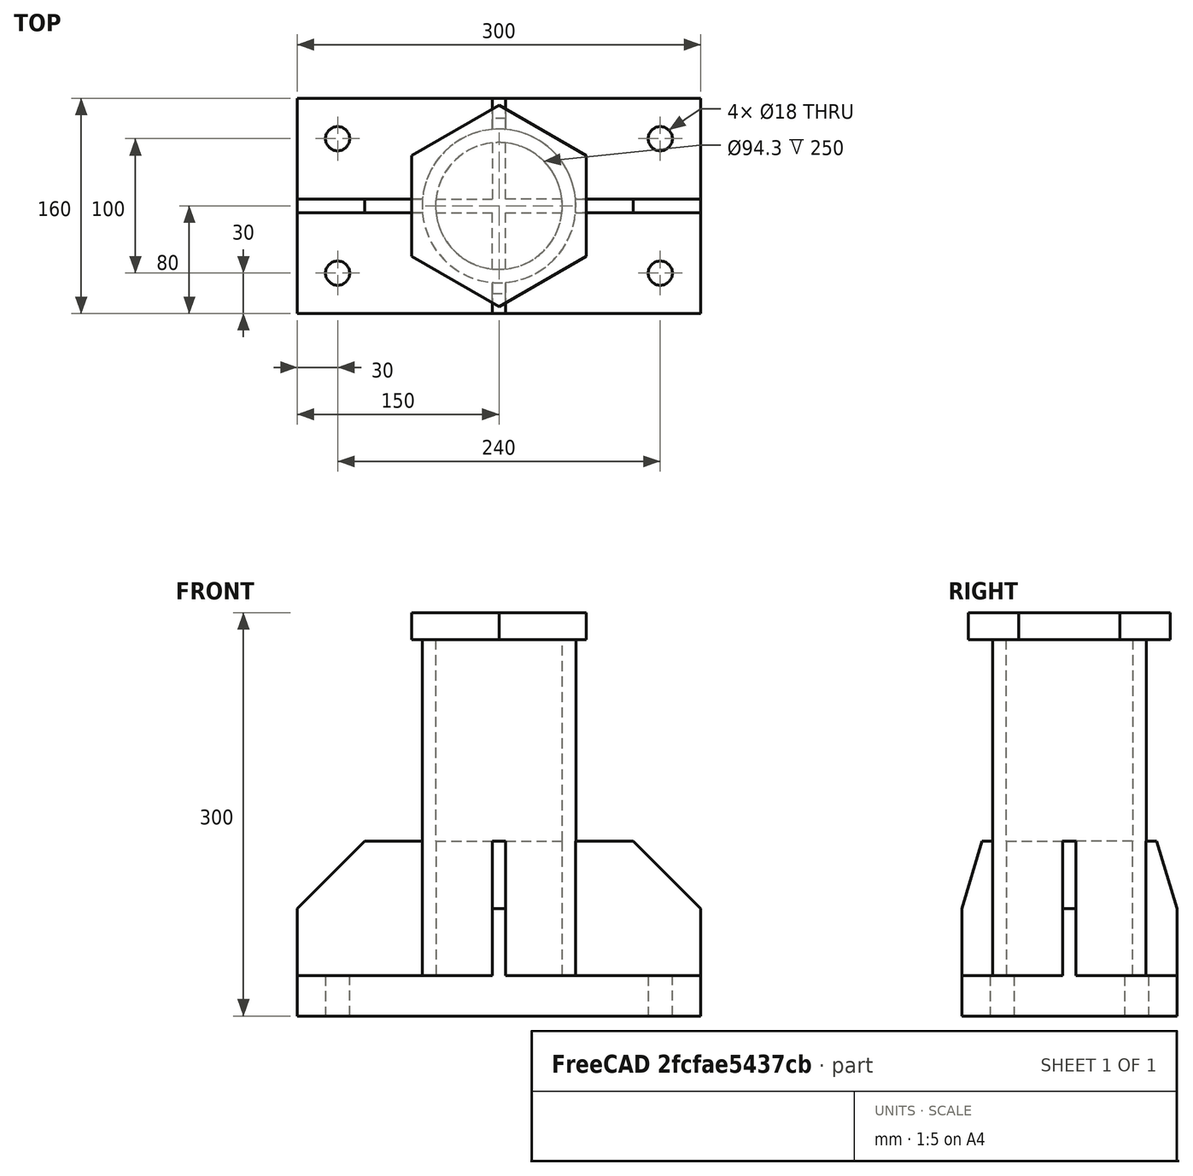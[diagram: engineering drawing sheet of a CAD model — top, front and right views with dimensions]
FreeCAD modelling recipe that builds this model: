
FCSTD DOCUMENT  (FreeCAD 0.21R33694 (Git))
Label: Anschluss_Rahmenfuss
License: All rights reserved
LicenseURL: http://en.wikipedia.org/wiki/All_rights_reserved
objects: Sketcher::SketchObject×5, Part::Extrusion×5, Fem::ConstraintForce×4, Part::MultiFuse×2, Fem::ConstraintFixed×2, Part::FeaturePython×1, Fem::FemSolverObjectPython×1, App::MaterialObjectPython×1, Part::Fillet×1, Fem::FemMeshObjectPython×1, Fem::FemAnalysis×1
note: 14 computed .brp shape members not serialized (recipe doc carries the construction recipe); baked Part::Feature solids carry a one-line shape summary decoded from their .brp

FEATURE [Sketcher::SketchObject] Sketch
  FullyConstrained = true
  sketch-geometry (12):
    g0: LineSegment StartX=-150 StartY=80 StartZ=0 EndX=150 EndY=80 EndZ=0
    g1: LineSegment StartX=150 StartY=80 StartZ=0 EndX=150 EndY=-80 EndZ=0
    g2: LineSegment StartX=150 StartY=-80 StartZ=0 EndX=-150 EndY=-80 EndZ=0
    g3: LineSegment StartX=-150 StartY=-80 StartZ=0 EndX=-150 EndY=80 EndZ=0
    g4: LineSegment StartX=-120 StartY=50 StartZ=0 EndX=120 EndY=50 EndZ=0
    g5: LineSegment StartX=120 StartY=50 StartZ=0 EndX=120 EndY=-50 EndZ=0
    g6: LineSegment StartX=120 StartY=-50 StartZ=0 EndX=-120 EndY=-50 EndZ=0
    g7: LineSegment StartX=-120 StartY=-50 StartZ=0 EndX=-120 EndY=50 EndZ=0
    g8: Circle CenterX=-120 CenterY=50 CenterZ=0 NormalX=0 NormalY=0 NormalZ=1 AngleXU=0 Radius=9
    g9: Circle CenterX=120 CenterY=50 CenterZ=0 NormalX=0 NormalY=0 NormalZ=1 AngleXU=0 Radius=9
    g10: Circle CenterX=120 CenterY=-50 CenterZ=0 NormalX=0 NormalY=0 NormalZ=1 AngleXU=0 Radius=9
    g11: Circle CenterX=-120 CenterY=-50 CenterZ=0 NormalX=0 NormalY=0 NormalZ=1 AngleXU=0 Radius=9
  constraints (28):
    c: Coincident(g0,g1)
    c: Coincident(g1,g2)
    c: Coincident(g2,g3)
    c: Coincident(g3,g0)
    c: Horizontal(g0)
    c: Vertical(g1)
    c: Symmetric(g2,g1,g-2)
    c: Symmetric(g2,g0,g-1)
    c: DistanceX(g2,g2) = 300
    c: DistanceY(g3,g3) = 160
    c: Coincident(g4,g5)
    c: Coincident(g5,g6)
    c: Coincident(g6,g7)
    c: Coincident(g7,g4)
    c: Horizontal(g4)
    c: Vertical(g5)
    c: Symmetric(g6,g5,g-2)
    c: Symmetric(g6,g4,g-1)
    c: DistanceX(g4,g4) = 240
    c: DistanceY(g5,g5) = 100
    c: Coincident(g8,g4)
    c: Coincident(g9,g4)
    c: Coincident(g10,g5)
    c: Coincident(g11,g6)
    c: Equal(g11,g10)
    c: Equal(g11,g9)
    c: Equal(g11,g8)
    c: Diameter(g11) = 18
FEATURE [Part::Extrusion] Extrude  label="platte"
  Base = -> Sketch
  Dir = (0,0,1)
  DirMode = 0
  FaceMakerClass = Part::FaceMakerBullseye
  LengthFwd = 30
  LengthRev = 0
  Solid = true
  Symmetric = false
FEATURE [Sketcher::SketchObject] Sketch001
  ExternalGeometry = -> [Extrude]
  FullyConstrained = true
  Placement = pos=(0,0,0) rot=(1,0,0;1.5708rad)
  sketch-geometry (6):
    g0: LineSegment StartX=150 StartY=30 StartZ=0 EndX=-150 EndY=30 EndZ=0
    g1: LineSegment StartX=-150 StartY=30 StartZ=0 EndX=-150 EndY=80 EndZ=0
    g2: LineSegment StartX=-150 StartY=80 StartZ=0 EndX=-100 EndY=130 EndZ=0
    g3: LineSegment StartX=-100 StartY=130 StartZ=0 EndX=100 EndY=130 EndZ=0
    g4: LineSegment StartX=100 StartY=130 StartZ=0 EndX=150 EndY=80 EndZ=0
    g5: LineSegment StartX=150 StartY=80 StartZ=0 EndX=150 EndY=30 EndZ=0
  constraints (16):
    c: Coincident(g-3,g0)
    c: Horizontal(g0)
    c: Coincident(g0,g1)
    c: Vertical(g1)
    c: Coincident(g1,g2)
    c: Coincident(g2,g3)
    c: Coincident(g3,g4)
    c: Coincident(g4,g5)
    c: Coincident(g5,g0)
    c: Vertical(g5)
    c: Equal(g1,g5)
    c: DistanceX(g0,g0) = 300
    c: Symmetric(g2,g3,g-2)
    c: DistanceX(g3,g3) = 200
    c: DistanceY(g5,g5) = 50
    c: DistanceY(g0,g3) = 100
FEATURE [Part::Extrusion] Extrude001  label="steife1"
  Base = -> Sketch001
  Dir = (0,-1,-3e-16)
  DirMode = 2
  FaceMakerClass = Part::FaceMakerBullseye
  LengthFwd = 10
  LengthRev = 0
  Solid = true
  Symmetric = true
FEATURE [Sketcher::SketchObject] Sketch002
  FullyConstrained = true
  MapMode = 5
  Placement = pos=(0,0,30) rot=(0,0,1;0rad)
  Support = -> [Extrude]
  sketch-geometry (3):
    g0: Circle CenterX=0 CenterY=0 CenterZ=0 NormalX=0 NormalY=0 NormalZ=1 AngleXU=0 Radius=57.15
    g1: Circle CenterX=0 CenterY=0 CenterZ=0 NormalX=0 NormalY=0 NormalZ=1 AngleXU=0 Radius=47.15
    g2: LineSegment StartX=47.15 StartY=0 StartZ=0 EndX=57.15 EndY=0 EndZ=0
  constraints (8):
    c: Coincident(g0,g-1)
    c: Diameter(g0) = 114.3
    c: Coincident(g1,g0)
    c: PointOnObject(g2,g1)
    c: PointOnObject(g2,g0)
    c: PointOnObject(g2,g-1)
    c: Horizontal(g2)
    c: DistanceX(g2,g2) = 10
FEATURE [Part::Extrusion] Extrude002  label="R114x10"
  Base = -> Sketch002
  Dir = (0,0,1)
  DirMode = 0
  FaceMakerClass = Part::FaceMakerBullseye
  LengthFwd = 270
  LengthRev = 0
  Solid = true
  Symmetric = false
FEATURE [Sketcher::SketchObject] Sketch003
  ExternalGeometry = -> [Extrude,Extrude001]
  FullyConstrained = true
  Placement = pos=(0,0,0) rot=(0.57735,0.57735,0.57735;2.0944rad)
  sketch-geometry (5):
    g0: LineSegment StartX=-80 StartY=30 StartZ=0 EndX=-80 EndY=80 EndZ=0
    g1: LineSegment StartX=-5 StartY=130 StartZ=0 EndX=-5 EndY=30 EndZ=0
    g2: LineSegment StartX=-5 StartY=30 StartZ=0 EndX=-80 EndY=30 EndZ=0
    g3: LineSegment StartX=-80 StartY=80 StartZ=0 EndX=-65 EndY=130 EndZ=0
    g4: LineSegment StartX=-65 StartY=130 StartZ=0 EndX=-5 EndY=130 EndZ=0
  constraints (13):
    c: Vertical(g1)
    c: Coincident(g1,g2)
    c: Coincident(g2,g0)
    c: Vertical(g0)
    c: Horizontal(g2)
    c: Coincident(g0,g3)
    c: Coincident(g3,g4)
    c: Coincident(g4,g1)
    c: Horizontal(g4)
    c: Coincident(g1,g-5)
    c: DistanceY(g0,g0) = 50
    c: DistanceX(g0,g3) = 15
    c: Coincident(g-3,g0)
FEATURE [Part::Extrusion] Extrude003  label="steife2"
  Base = -> Sketch003
  Dir = (1,0,0)
  DirMode = 2
  FaceMakerClass = Part::FaceMakerBullseye
  LengthFwd = 10
  LengthRev = 0
  Solid = true
  Symmetric = true
FEATURE [Part::FeaturePython] Clone  label="steife003"  # Draft clone (typed FeaturePython)
  AttacherType = Attacher::AttachEngine3D
  Fuse = false
  Objects = -> [Extrude003]
  Placement = pos=(0,0,0) rot=(0,0,1;3.14159rad)
  Scale = (1,1,1)
FEATURE [Part::MultiFuse] Fusion  label="bauteil"
  Refine = true
  Shapes = -> [Extrude,Extrude001,Extrude002,Extrude003,Clone]
FEATURE [Sketcher::SketchObject] Sketch004
  FullyConstrained = true
  MapMode = 5
  Placement = pos=(0,0,300) rot=(0,0,1;0rad)
  Support = -> [Fusion]
  sketch-geometry (7):
    g0: LineSegment StartX=65 StartY=37.5278 StartZ=0 EndX=0 EndY=75.0555 EndZ=0
    g1: LineSegment StartX=0 StartY=75.0555 StartZ=0 EndX=-65 EndY=37.5278 EndZ=0
    g2: LineSegment StartX=-65 StartY=37.5278 StartZ=0 EndX=-65 EndY=-37.5278 EndZ=0
    g3: LineSegment StartX=-65 StartY=-37.5278 StartZ=0 EndX=0 EndY=-75.0555 EndZ=0
    g4: LineSegment StartX=0 StartY=-75.0555 StartZ=0 EndX=65 EndY=-37.5278 EndZ=0
    g5: LineSegment StartX=65 StartY=-37.5278 StartZ=0 EndX=65 EndY=37.5278 EndZ=0
    g6: Circle CenterX=0 CenterY=0 CenterZ=0 NormalX=0 NormalY=0 NormalZ=1 AngleXU=0 Radius=75.0555
  constraints (16):
    c: Coincident(g0,g1)
    c: Coincident(g1,g2)
    c: Coincident(g2,g3)
    c: Coincident(g3,g4)
    c: Coincident(g4,g5)
    c: Coincident(g5,g0)
    c: Equal(g0, g1-g5) x5
    c: PointOnObject(g0,g6)
    c: PointOnObject(g1,g6)
    c: PointOnObject(g2,g6)
    c: PointOnObject(g3,g6)
    c: PointOnObject(g4,g6)
    c: PointOnObject(g5,g6)
    c: Coincident(g6,g-1)
    c: Vertical(g5)
    c: DistanceX(g1,g0) = 130
FEATURE [Part::Extrusion] Extrude004  label="lastplatte"
  Base = -> Sketch004
  Dir = (0,0,-1)
  DirMode = 0
  FaceMakerClass = Part::FaceMakerBullseye
  LengthFwd = 20
  LengthRev = 0
  Solid = true
  Symmetric = false
FEATURE [Part::MultiFuse] Fusion001
  Refine = true
  Shapes = -> [Fusion,Extrude004]
FEATURE [Fem::FemSolverObjectPython] SolverCcxTools  # FEM object (typed FeaturePython)
  AnalysisType = 0
  BeamShellResultOutput3D = true
  BucklingFactors = 1
  EigenmodeHighLimit = 1000000
  EigenmodeLowLimit = 0
  EigenmodesCount = 10
  GeometricalNonlinearity = 1
  IterationsControlParameterCutb = 0.25,0.5,0.75,0.85,,,1.5,
  IterationsControlParameterIter = 4,8,9,200,10,400,,200,,
  IterationsControlParameterTimeUse = false
  IterationsThermoMechMaximum = 2000
  IterationsUserDefinedIncrementations = false
  IterationsUserDefinedTimeStepLength = false
  MaterialNonlinearity = 1
  MatrixSolverType = 0
  SplitInputWriter = true
  ThermoMechSteadyState = true
  TimeEnd = 1
  TimeInitialStep = 0.01
FEATURE [App::MaterialObjectPython] MaterialSolid  label="S355"  # material (typed FeaturePython)
  Category = 0
  Material = AuthorAndLicense=(c) 2013 Juergen Riegel (CC-BY 3.0),CardName=CalculiX-Steel,Density=7900 kg/m^3,+8 more (map truncated)
FEATURE [Fem::ConstraintFixed] ConstraintFixed
  NormalDirection = (1,-1e-16,0)
  Normals = (32) [(-1,0,0),(0.5,-0.866025,0),(0.5,0.866025,0),(-1,2.44929e-16,0),(-1,0,0),(0.5,-0.866025,0),(0.5,0.866025,0),(-1,2.44929e-16,0),(-1,0,0),+23 more]
  Points = (32) [(-111,-50,30),(-124.5,-42.2058,30),(-124.5,-57.7942,30),(-111,-50,30),(-111,-50,20),(-124.5,-42.2058,20),(-124.5,-57.7942,20),(-111,-50,20),+24 more]
  References = -> [Fusion001]
  Scale = 5
FEATURE [Fem::ConstraintFixed] ConstraintFixed001
  NormalDirection = (1,-1e-16,0)
  Normals = (32) [(-1,0,0),(0.5,-0.866025,0),(0.5,0.866025,0),(-1,2.44929e-16,0),(-1,0,0),(0.5,-0.866025,0),(0.5,0.866025,0),(-1,2.44929e-16,0),(-1,0,0),+23 more]
  Points = (32) [(129,-50,30),(115.5,-42.2058,30),(115.5,-57.7942,30),(129,-50,30),(129,-50,20),(115.5,-42.2058,20),(115.5,-57.7942,20),(129,-50,20),(129,-50,10),+23 more]
  References = -> [Fusion001]
  Scale = 5
FEATURE [Fem::ConstraintForce] ConstraintForce  label="Q"
  Direction = -> Fusion001 [Edge67]
  DirectionVector = (1,0,0)
  Force = 31900
  NormalDirection = (0,0,1)
  Points = (8) [(-65,-25.0185,300),(-21.6667,-25.0185,300),(21.6667,-25.0185,300),(65,-25.0185,300),(-65,25.0185,300),(-21.6667,25.0185,300),(21.6667,25.0185,300),+1 more]
  References = -> [Fusion001]
  Reversed = true
  Scale = 12
FEATURE [Fem::ConstraintForce] ConstraintForce001  label="N"
  DirectionVector = (0,0,1)
  Force = 40500
  NormalDirection = (0,0,1)
  Points = (8) [(-65,-25.0185,300),(-21.6667,-25.0185,300),(21.6667,-25.0185,300),(65,-25.0185,300),(-65,25.0185,300),(-21.6667,25.0185,300),(21.6667,25.0185,300),+1 more]
  References = -> [Fusion001]
  Scale = 12
FEATURE [Fem::ConstraintForce] ConstraintForce002  label="V1"
  Direction = -> Fusion001 [Edge36]
  DirectionVector = (0,0,-1)
  Force = 96000
  NormalDirection = (1,0,0)
  Points = (12) [(65,-37.5278,280),(65,-12.5093,280),(65,12.5093,280),(65,37.5278,280),(65,-37.5278,290),(65,-12.5093,290),(65,12.5093,290),(65,37.5278,290),+4 more]
  References = -> [Fusion001]
  Reversed = true
  Scale = 6
FEATURE [Fem::ConstraintForce] ConstraintForce003  label="V2"
  Direction = -> Fusion001 [Edge70]
  DirectionVector = (0,0,1)
  Force = 96000
  NormalDirection = (-1,-2e-16,0)
  Points = (12) [(-65,37.5278,280),(-65,12.5093,280),(-65,-12.5093,280),(-65,-37.5278,280),(-65,37.5278,290),(-65,12.5093,290),(-65,-12.5093,290),(-65,-37.5278,290),+4 more]
  References = -> [Fusion001]
  Scale = 6
FEATURE [Part::Fillet] Fillet
  Base = -> Fusion001
  Edges = 1 edges r=1: [Edge27]
FEATURE [Fem::FemMeshObjectPython] FEMMeshGmsh  # FEM object (typed FeaturePython)
  Algorithm2D = 0
  Algorithm3D = 0
  CharacteristicLengthMax = 8
  CharacteristicLengthMin = 0
  CoherenceMesh = true
  ElementDimension = 0
  ElementOrder = 1
  GeometryTolerance = 1e-06
  GroupsOfNodes = false
  HighOrderOptimize = 0
  MeshSizeFromCurvature = 12
  OptimizeNetgen = false
  OptimizeStd = true
  Part = -> Fillet
  RecombinationAlgorithm = 0
  Recombine3DAll = false
  RecombineAll = false
  SecondOrderLinear = false
FEATURE [Fem::FemAnalysis] Analysis
  Group = -> [SolverCcxTools,MaterialSolid,ConstraintFixed,ConstraintFixed001,ConstraintForce,ConstraintForce001,ConstraintForce002,ConstraintForce003,FEMMeshGmsh]
